# Revit family: Насадки с барьерами
name_source: partatom
category: Специальное оборудование
units: mm (PartAtom-declared; Revit-internal decimal feet)

## family parameters
Общий = Нет
При загрузке вырезать с полостями = Нет
Размер круглого соединителя = Использовать диаметр
Тип детали = Нормальный
Точка расчета площади = Нет

## types (15) — shared parameters
ADSK_Единица измерения = м.
ADSK_Завод-изготовитель = FENSYS
URL = https://www.fensys.ru
Группа модели = Насадки
Изготовитель = FENSYS
Крепление насадок барьерам = 5

## per-type parameters (varying)
| type | ADSK_Наименование | Y насадка | Видимость ПББ | Высота ПББ | Левая | Насадка I | ПББ левая | ПББ правая | Правая | СББ | Ф СББ |
| Насадки V СББ 500 | Насадки на ограждения V-образные с СББ | Да | Нет | 500 мм | Да | Нет | Нет | Нет | Да | Да | 500 мм |
| Насадки L левая ПББ 500 | Насадки на ограждения L-образные | Нет | Да | 500 мм | Да | Нет | Да | Нет | Нет | Нет | 500 мм |
| Насадки L правая ПББ 500 | Насадки на ограждения L-образные | Нет | Да | 500 мм | Нет | Нет | Нет | Да | Да | Нет | 500 мм |
| Насадка I ПББ 500 | Насадки на ограждения I-образные | Нет | Да | 500 мм | Нет | Да | Нет | Нет | Нет | Нет | 500 мм |
| Насадки V ПББ 500 | Насадки на ограждения V-образные с ПББ | Да | Да | 500 мм | Да | Нет | Да | Да | Да | Нет | 500 мм |
| Насадка I ПББ 600 | Насадки на ограждения I-образные | Нет | Да | 600 мм | Нет | Да | Нет | Нет | Нет | Нет | 500 мм |
| Насадка I ПББ 900 | Насадки на ограждения I-образные | Нет | Да | 900 мм | Нет | Да | Нет | Нет | Нет | Нет | 500 мм |
| Насадки L левая ПББ 600 | Насадки на ограждения L-образные | Нет | Да | 600 мм | Да | Нет | Да | Нет | Нет | Нет | 500 мм |
| Насадки L левая ПББ 900 | Насадки на ограждения L-образные | Нет | Да | 900 мм | Да | Нет | Да | Нет | Нет | Нет | 500 мм |
| Насадки L правая ПББ 600 | Насадки на ограждения L-образные | Нет | Да | 600 мм | Нет | Нет | Нет | Да | Да | Нет | 500 мм |
| Насадки L правая ПББ 900 | Насадки на ограждения L-образные | Нет | Да | 900 мм | Нет | Нет | Нет | Да | Да | Нет | 500 мм |
| Насадки V ПББ 600 | Насадки на ограждения V-образные с ПББ | Да | Да | 600 мм | Да | Нет | Да | Да | Да | Нет | 500 мм |
| Насадки V ПББ 900 | Насадки на ограждения V-образные с ПББ | Да | Да | 900 мм | Да | Нет | Да | Да | Да | Нет | 500 мм |
| Насадки V СББ 600 | Насадки на ограждения V-образные с СББ | Да | Нет | 600 мм | Да | Нет | Нет | Нет | Да | Да | 600 мм |
| Насадки V СББ 900 | Насадки на ограждения V-образные с СББ | Да | Нет | 900 мм | Да | Нет | Нет | Нет | Да | Да | 900 мм |
